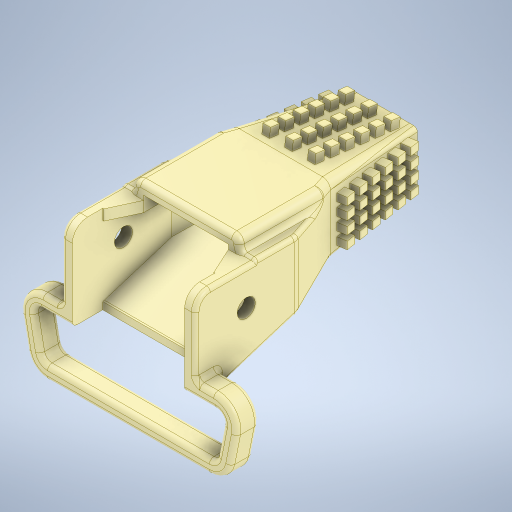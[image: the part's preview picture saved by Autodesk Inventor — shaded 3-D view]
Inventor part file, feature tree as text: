
AUTODESK INVENTOR PART (.ipt)
format: ipt  version: 2024 (Build 280153000, 153)  size: 1,475,584 bytes
history: native  units: mm
features: projected_geometry x19, sketch x9, extrude x7, plane x5, loft x2, other x2, fillet x1, mirror x1
ambient origin geometry x8: Origin, YZ Plane, XZ Plane, XY Plane, X Axis, Y Axis, Z Axis, Center Point
bodies: Solid1 (feature_tree), Solid2 (feature_tree)
feature tree (46):
  plane  "Work Plane6"
  loft  "Loft3"
  loft  "Loft4"
  fillet  "Fillet6"  [1 undecoded]
  sketch  "Sketch46"  dims[d156=9.5mm d157=4.75mm]
  extrude  "Grippers"  Depth=2.45mm
  mirror  "Mirror1"
  sketch  "Sketch47"  dims[d158=10.5mm d159=5.25mm]
  extrude  "FrontGrippers"  TaperAngle=0.0deg  [1 undecoded]
  sketch  "Sketch49"  dims[d160=12.5mm d162=11.5mm d284=0.0mm d287=0.45mm d288=0.5mm d296=40.0mm d298=2.5mm d299=60.0mm d301=5.0mm d363=0.5mm d364=0.6mm d416=0.6mm d417=0.0mm d425=0.5mm d426=60.0mm d428=5.0mm d429=10.0mm d431=10.0mm d433=20.0mm d435=1.5mm d436=20.0mm d438=1.5mm d441=0.6mm d442=0.0mm d444=6.25mm d445=5.75mm d447=0.25mm d39=0.5mm d40=0.872665mm d41=0.5mm d42=0.872665mm d193=0.5mm d194=0.872665mm d195=0.5mm d196=0.872665mm]
  extrude  "BackGrippers"  Depth=15.0mm TaperAngle=0.0deg
  plane  "Work Plane13"
  plane  "Work Plane14"
  extrude  "Extrusion16"  Depth=15.0mm TaperAngle=0.0deg
  extrude  "Extrusion19"  Depth=4.75mm
  extrude  "Extrusion21"  Depth=5.25mm
  extrude  "Extrusion22"  Depth=0.5mm
  plane  "Work Plane4"
  plane  "Work Plane5"
  sketch  "Sketch5"  dims[d20=-7.1mm d22=4.5mm]
  other  "Edges3"
  sketch  "Sketch7"  dims[d23=3.5mm d24=0.0mm d25=90.0deg d26=0.0mm d27=90.0deg]
  other  "Edges4"
  sketch  "Sketch22"  dims[d28=2.85mm d29=2.45mm]
  projected_geometry  "Projected Loop8"
  sketch  "Sketch25"  dims[d30=0.0mm d31=90.0deg d32=0.0mm d33=90.0deg]
  sketch  "Sketch27"  dims[d126=1.0mm d127=0.0mm d135=15.0mm d136=0.0mm]
  sketch  "Sketch28"  dims[d140=1.0mm d141=0.0mm d142=15.0mm d143=0.0mm]
  projected_geometry  "Projected Loop36"
  projected_geometry  "Projected Loop37"
  projected_geometry  "Projected Loop38"
  projected_geometry  "Projected Loop39"
  projected_geometry  "Projected Loop40"
  projected_geometry  "Projected Loop41"
  projected_geometry  "Projected Loop42"
  projected_geometry  "Projected Loop43"
  projected_geometry  "Projected Loop44"
  projected_geometry  "Projected Loop45"
  projected_geometry  "Projected Loop46"
  projected_geometry  "Projected Loop47"
  projected_geometry  "Projected Loop48"
  projected_geometry  "Projected Loop49"
  projected_geometry  "Projected Loop50"
  projected_geometry  "Projected Loop51"
  projected_geometry  "Projected Loop52"
  projected_geometry  "Projected Loop53"
note: 2 required parameter values undecoded (feature->parameter linkage not recoverable at this tier; creation-order binding heuristic only, values carry confidence <= 0.55)
